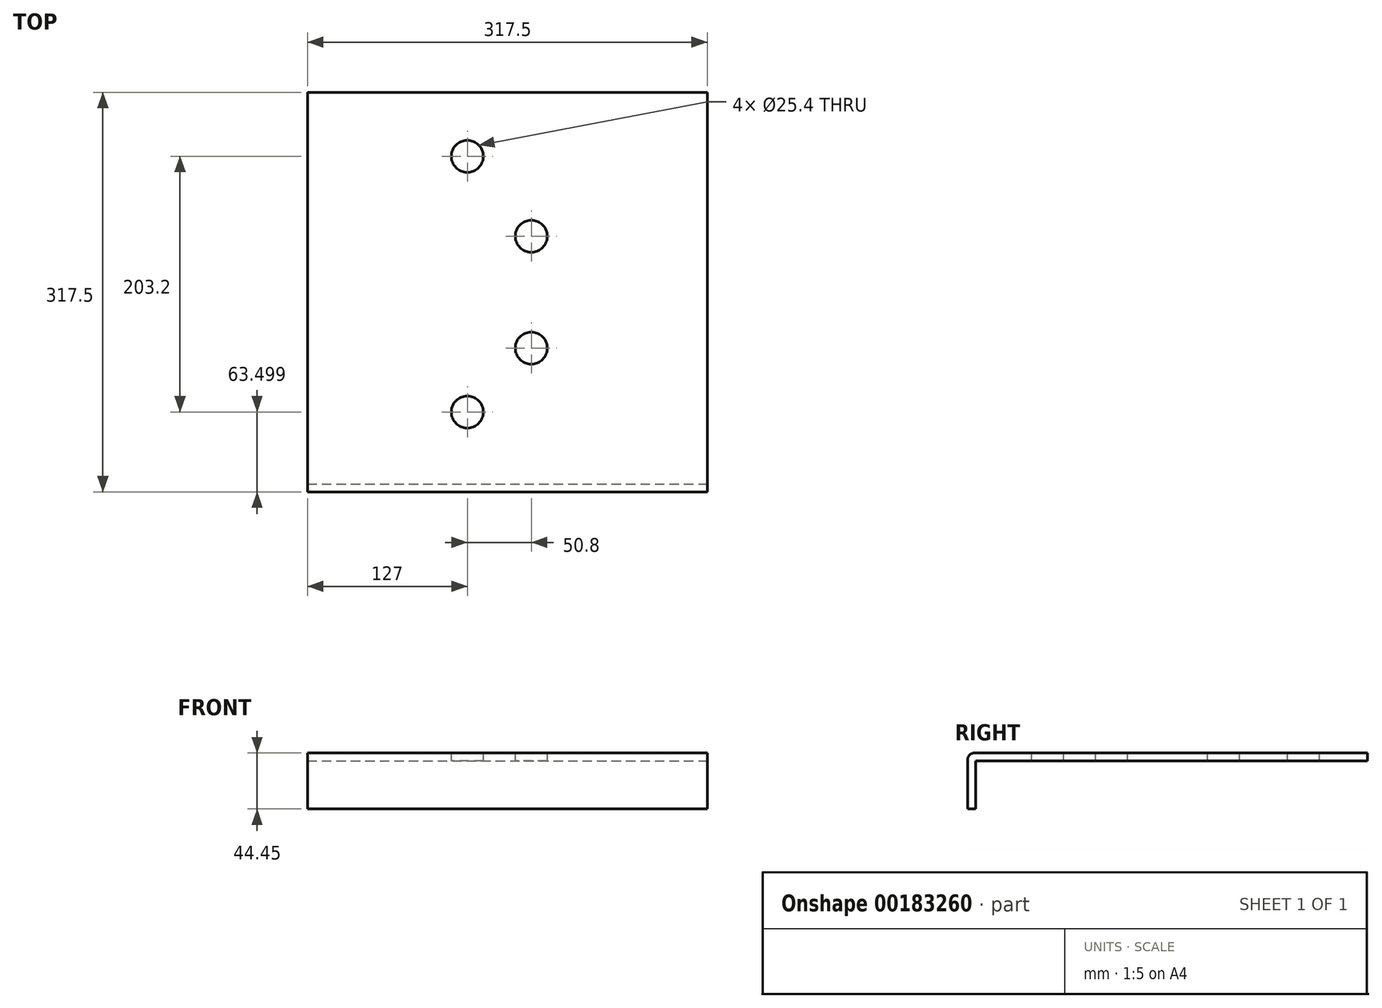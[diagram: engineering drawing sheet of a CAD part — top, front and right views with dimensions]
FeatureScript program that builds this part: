
annotation { "Feature Type Name" : "Feature", "Feature Type Description" : "" }
export const myFeature = defineFeature(function(context is Context, id is Id, definition is map)
    precondition{}
    {
        {
            var Q0;
            Q0=qCreatedBy(makeId("Top.planeOp"),FACE);
            var sketch = newSketch(context, id + "F0", { "sketchPlane" : qUnion([Q0])});
            skLineSegment(sketch, "E0.bottom", {"start": v(0, 13.78) * mm, "end": v(317.5, 13.78) * mm});
            skLineSegment(sketch, "E0.top", {"start": v(0, 331.28) * mm, "end": v(317.5, 331.28) * mm});
            skLineSegment(sketch, "E0.left", {"start": v(0, 13.78) * mm, "end": v(0, 331.28) * mm});
            skLineSegment(sketch, "E0.right", {"start": v(317.5, 13.78) * mm, "end": v(317.5, 331.28) * mm});
            skSolve(sketch);
        }
        {
            var Q0;
            Q0=makeQuery(id+"F0.imprint","IMPRINT",FACE,{"disambiguationData":[TD([[makeQuery(id+"F0.imprint","IMPRINT",EDGE,{"derivedFrom":sQuery(id+"F0.wireOp",EDGE,"E0.bottom")}),1.0]])]});
            extrude(context, id + "F1", {"entities" : qUnion([Q0]), "depth" : 6.35 * mm});
        }
        {
            var Q0;
            Q0=makeQuery(id+"F1.opExtrude","CAP_FACE",FACE,{"disambiguationData":[OSD([sQuery(id+"F0.wireOp",EDGE,"E0.bottom"),sQuery(id+"F0.wireOp",EDGE,"E0.top"),sQuery(id+"F0.wireOp",EDGE,"E0.left"),sQuery(id+"F0.wireOp",EDGE,"E0.right")])],"isStart":true});
            var sketch = newSketch(context, id + "F2", { "sketchPlane" : qUnion([Q0])});
            skLineSegment(sketch, "E1.bottom", {"start": v(0, -13.78) * mm, "end": v(317.5, -13.78) * mm});
            skLineSegment(sketch, "E1.top", {"start": v(0, -20.13) * mm, "end": v(317.5, -20.13) * mm});
            skLineSegment(sketch, "E1.left", {"start": v(0, -13.78) * mm, "end": v(0, -20.13) * mm});
            skLineSegment(sketch, "E1.right", {"start": v(317.5, -13.78) * mm, "end": v(317.5, -20.13) * mm});
            skSolve(sketch);
        }
        {
            var Q0;
            Q0=makeQuery(id+"F2.imprint","IMPRINT",FACE,{"disambiguationData":[TD([[makeQuery(id+"F2.imprint","IMPRINT",EDGE,{"derivedFrom":sQuery(id+"F2.wireOp",EDGE,"E1.bottom")}),-1.0]])]});
            extrude(context, id + "F3", {"entities" : qUnion([Q0]), "operationType" : NewBodyOperationType.ADD, "depth" : 38.1 * mm});
        }
        {
            var Q0;
            Q0=makeQuery(id+"F1.opExtrude","CAP_EDGE",EDGE,{"disambiguationData":[OSD([sQuery(id+"F0.wireOp",EDGE,"E0.bottom")])],"isStart":false});
            var Q1;
            Q1=makeQuery(id+"F3.opExtrude","CAP_EDGE",EDGE,{"disambiguationData":[OSD([sQuery(id+"F2.wireOp",EDGE,"E1.top")])],"isStart":true});
            fillet(context, id + "F4", {"entities" : qUnion([Q0, Q1]), "radius" : 5.08 * mm, "tangentPropagation" : true, "allowEdgeOverflow" : false});
        }
        {
            var Q0;
            Q0=makeQuery(id+"F1.opExtrude","CAP_FACE",FACE,{"disambiguationData":[OSD([sQuery(id+"F0.wireOp",EDGE,"E0.bottom"),sQuery(id+"F0.wireOp",EDGE,"E0.top"),sQuery(id+"F0.wireOp",EDGE,"E0.left"),sQuery(id+"F0.wireOp",EDGE,"E0.right")])],"isStart":false});
            var sketch = newSketch(context, id + "F5", { "sketchPlane" : qUnion([Q0])});
            skCircle(sketch, "E2", {"center": v(127, 77.28) * mm, "radius": 12.7 * mm});
            skCircle(sketch, "E3", {"center": v(177.8, 128.08) * mm, "radius": 12.7 * mm});
            skCircle(sketch, "E4", {"center": v(177.8, 216.98) * mm, "radius": 12.7 * mm});
            skCircle(sketch, "E5", {"center": v(127, 280.48) * mm, "radius": 12.7 * mm});
            skSolve(sketch);
        }
        {
            var Q0;
            Q0=makeQuery(id+"F5.imprint","IMPRINT",FACE,{"disambiguationData":[TD([[makeQuery(id+"F5.imprint","IMPRINT",EDGE,{"derivedFrom":sQuery(id+"F5.wireOp",EDGE,"E2")}),1.0]])]});
            var Q1;
            Q1=makeQuery(id+"F5.imprint","IMPRINT",FACE,{"disambiguationData":[TD([[makeQuery(id+"F5.imprint","IMPRINT",EDGE,{"derivedFrom":sQuery(id+"F5.wireOp",EDGE,"E3")}),1.0]])]});
            var Q2;
            Q2=makeQuery(id+"F5.imprint","IMPRINT",FACE,{"disambiguationData":[TD([[makeQuery(id+"F5.imprint","IMPRINT",EDGE,{"derivedFrom":sQuery(id+"F5.wireOp",EDGE,"E4")}),1.0]])]});
            var Q3;
            Q3=makeQuery(id+"F5.imprint","IMPRINT",FACE,{"disambiguationData":[TD([[makeQuery(id+"F5.imprint","IMPRINT",EDGE,{"derivedFrom":sQuery(id+"F5.wireOp",EDGE,"E5")}),1.0]])]});
            extrude(context, id + "F6", {"entities" : qUnion([Q0, Q1, Q2, Q3]), "operationType" : NewBodyOperationType.REMOVE, "oppositeDirection" : true, "depth" : 25.4 * mm});
        }
    });
